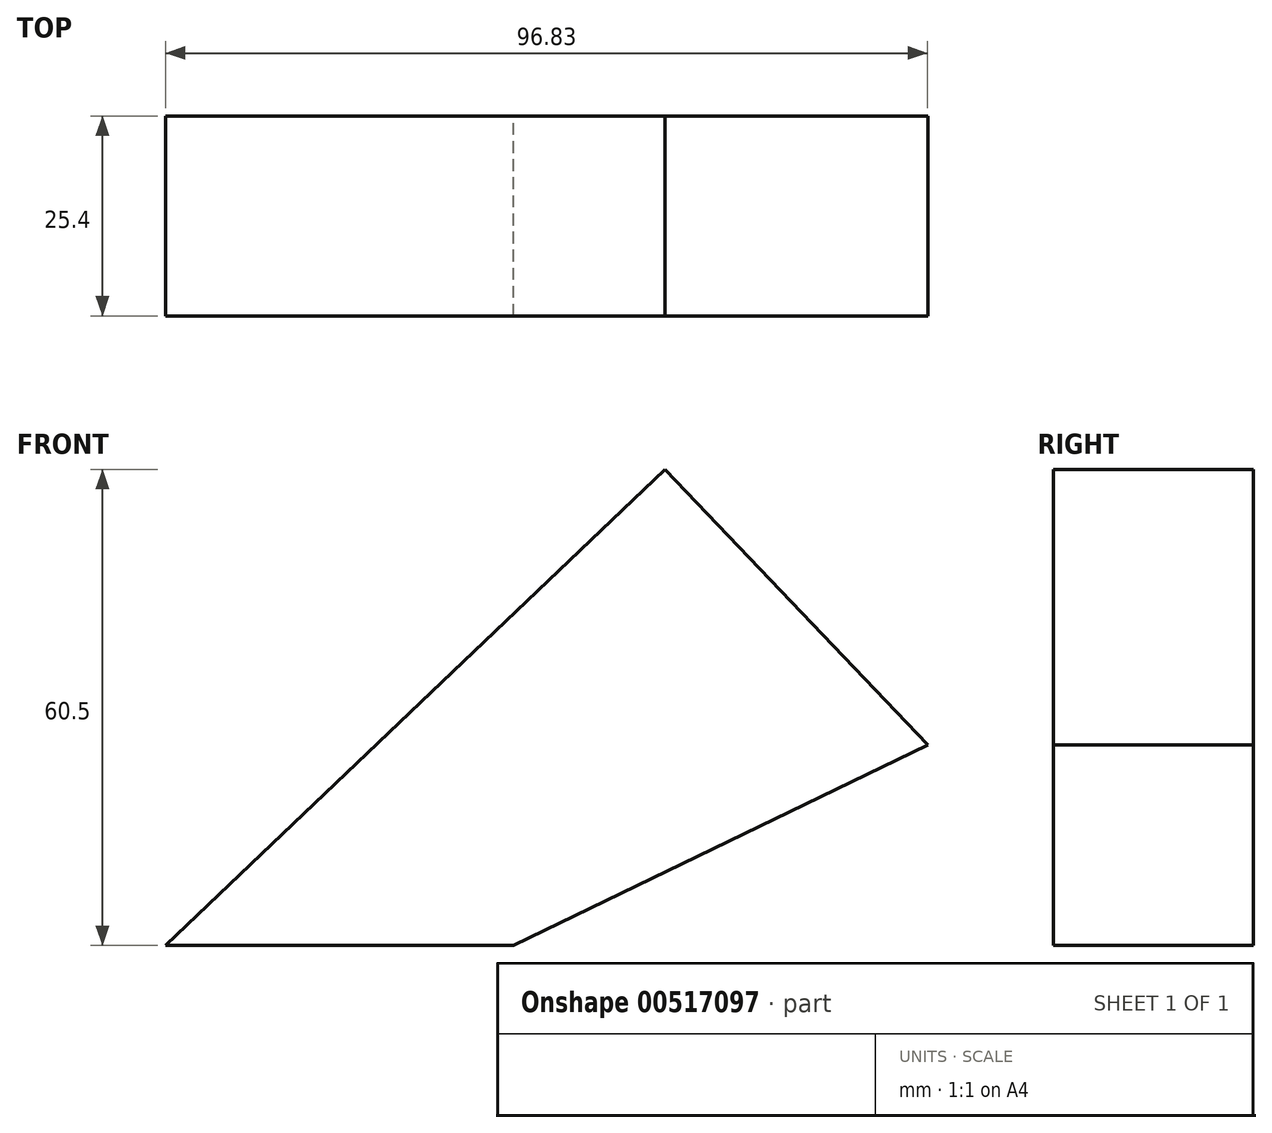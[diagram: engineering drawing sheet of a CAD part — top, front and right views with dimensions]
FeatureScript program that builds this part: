
annotation { "Feature Type Name" : "Feature", "Feature Type Description" : "" }
export const myFeature = defineFeature(function(context is Context, id is Id, definition is map)
    precondition{}
    {
        {
            var Q0;
            Q0=qCreatedBy(makeId("Front.planeOp"),FACE);
            var sketch = newSketch(context, id + "F0", { "sketchPlane" : qUnion([Q0])});
            skLineSegment(sketch, "E0", {"start": v(-60.51, 25.22) * mm, "end": v(-44.2, 0) * mm});
            skLineSegment(sketch, "E1", {"start": v(-44.2, 0) * mm, "end": v(19.27, 60.5) * mm});
            skLineSegment(sketch, "E2", {"start": v(19.27, 60.5) * mm, "end": v(52.62, 25.5) * mm});
            skLineSegment(sketch, "E3", {"start": v(52.62, 25.5) * mm, "end": v(0, 0) * mm});
            skLineSegment(sketch, "E4", {"start": v(0, 0) * mm, "end": v(-44.2, 0) * mm});
            skSolve(sketch);
        }
        {
            var Q0;
            Q0 = qSketchRegion(id + "F0", true);
            extrude(context, id + "F1", {"entities" : qUnion([Q0]), "depth" : 25.4 * mm, "offsetDistance" : 25.4 * mm});
        }
    });
